# Revit family: ASH_Contour21_S6454_BIM_GB
name_source: partatom
category: Plumbing Fixtures
revit_build: Autodesk Revit MEP 2012 (Build: 20110309_2315(x64)
units: mm (PartAtom-declared; Revit-internal decimal feet)

## types (5) — shared parameters
AccessibilityPerformance = DDA Compliant
Accessories = www.idealspec.co.uk
Assembly Code = C1030200
AssetType = Fixed
BIMObjectName = GRABRAIL_ArmitageShanks-Contour21-Straight60cm_S6454
BREEAM Approved = No
Brand = Armitage Shanks
Category = Furniture_GRABRAIL_UK
ConnectionType = Mechanical
CurrentRevision = 1
Default Elevation = 1219 mm
Description = Contour 21 grab rail straight 60cm long x 35mm diameter
DurationUnit = Years
ECA = No
ElementType = GRAB RAIL: Safety device to aid maintaining balance, lessen fatigue and assist in supporting weight whilst maneuvering the body
ExpectedLife = 30
Help = http://www.idealspec.co.uk
InstallationInstructions = http://www.idealspec.co.uk
Manufacturer = Ideal Standard International Ltd
ManufacturerURL = www.idealspec.co.uk
Name = GRABRAIL_ArmitageShanks-Contour21-Straight60cm_S6454
NettWeight = 2Kg
NominalHeight = 118 mm
NominalLength = 600 mm
NominalWidth = 84 mm
PredefinedType = grabrail
ProductDataSheet = http://www.idealspec.co.uk
ProductInformation = http://www.idealspec.co.uk
SalesInformation = http://www.idealspec.co.uk
SendEnquiry = http://www.idealspec.co.uk
Shape = Tubular
Size = mm x mm x mm
Space = Internal
SpareParts = www.fastpart-spares.co.uk
StandardsConformance = DDA, Doc-M
URL = www.idealspec.co.uk
Version = 2
VolumeUnits = Litres
WRAS = No
WarrantyDescription = Manufacturers Warranty
WarrantyDurationParts = 5
WarrantyDurationUnit = Years
WarrantyGuarantorParts = Ideal Standard International Ltd
WaterEfficientProduct = No

## per-type parameters (varying)
| type | BarCode | Colour | Features | Finish | Grade | LRVValue | Material | Model | ModelNumber | ModelReference | RAL |
| S6454LI | 5017830384885 | Powder Coated Aluminium Blue LI | straight 60cm long x 35mm diameter Blue | Powder Coated Aluminium Blue LI | T6 | 27 | Aluminium | S645436 | S645436 | S645436 | 5011 |
| S645401 | 5017830383772 | Powder Coated Aluminium White 01 | Straight 60cm Long x 35mm diameter | Powder Coated Aluminium White 01 | T6 | 94 | Alumnium | S6454AC | S6454AC | S6454AC | 9016 |
| S6454LJ | 5017830384564 | Powder Coated Aluminium Grey LJ | straight 60cm long x 35mm diameter Light Grey | Powder Coated Aluminium Grey LJ | T6 | 20 | Aluminium | S6454LJ | S6454LJ | S6454LJ | 7005 |
| S6454RN | 5017830388425 | Powder Coated Aluminium Charcoal RN | straight 60cm long x 35mm diameter Charcoal | Powder Coated Aluminium Charcoal RN | T6 | 9 | Aluminium | S6454RN | S6454RN | S6454RN | 7016 |
| S6454MY | 5017830384243 | Stainless Steel MY | straight 60cm long x 35mm diameter Stainless Steel | Polished | 304 |  | Stainless Steel | S6454MY | S6454MY | S6454MY |  |

note: column(s) folded — value = type name in every type: PartNumber

## geometry (parser evidence)
native form markers: Blend x9, Sweep x3
no freeform markers — native parametric forms only
